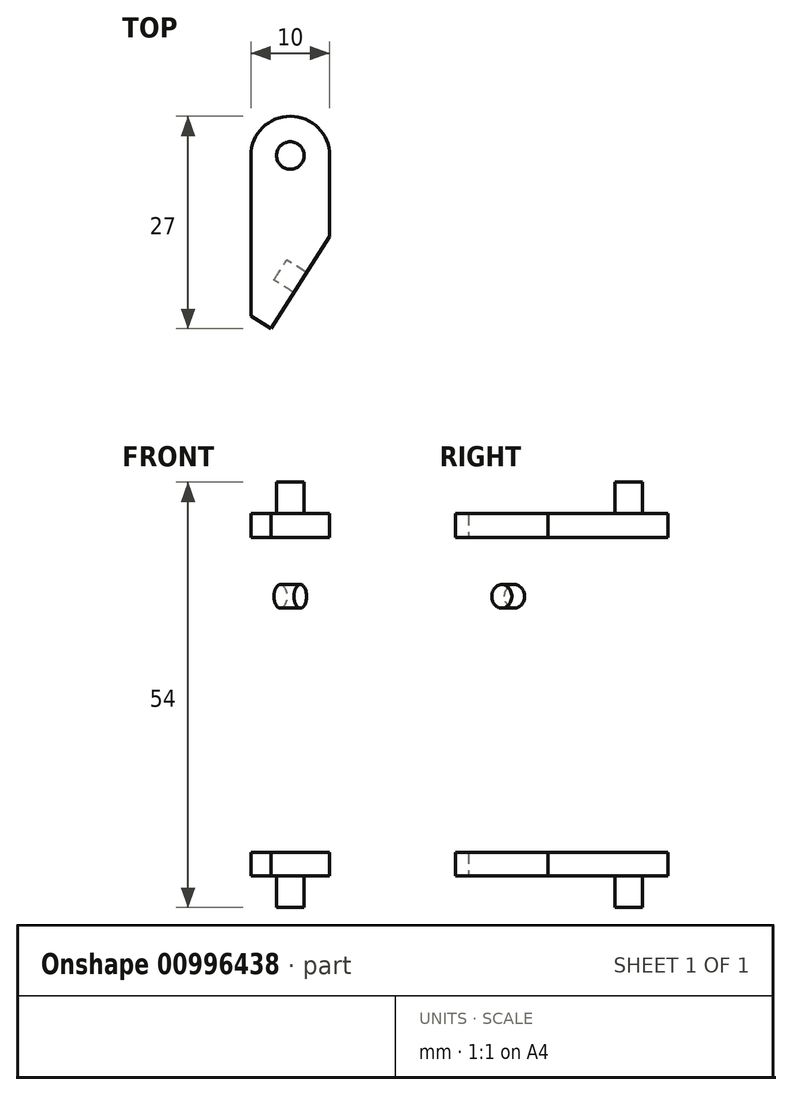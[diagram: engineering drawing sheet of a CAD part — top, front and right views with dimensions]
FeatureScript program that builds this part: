
annotation { "Feature Type Name" : "Feature", "Feature Type Description" : "" }
export const myFeature = defineFeature(function(context is Context, id is Id, definition is map)
    precondition{}
    {
        {
            var Q0;
            Q0=qCreatedBy(makeId("Top.planeOp"),FACE);
            var sketch = newSketch(context, id + "F0", { "sketchPlane" : qUnion([Q0])});
            skArc(sketch, "E0", {"start": v(5, 0) * mm, "mid": v(0, 5) * mm, "end": v(-5, 0) * mm});
            skCircle(sketch, "E1", {"center": v(0, 0) * mm, "radius": 1.75 * mm});
            skLineSegment(sketch, "E2", {"start": v(-5, 0) * mm, "end": v(-5, -20.39) * mm});
            skLineSegment(sketch, "E3", {"start": v(5, 0) * mm, "end": v(5, -10.27) * mm});
            skLineSegment(sketch, "E4", {"start": v(-5, -20.39) * mm, "end": v(-2.47, -22) * mm});
            skLineSegment(sketch, "E5", {"start": v(-2.47, -22) * mm, "end": v(5, -10.27) * mm});
            skLineSegment(sketch, "E6", {"start": v(0, 5) * mm, "end": v(0, -22) * mm, "construction": true});
            skLineSegment(sketch, "E7", {"start": v(-5, -20.39) * mm, "end": v(2.47, -8.66) * mm});
            skLineSegment(sketch, "E8", {"start": v(2.47, -8.66) * mm, "end": v(5, -10.27) * mm});
            skSolve(sketch);
        }
        {
            var Q0;
            Q0=makeQuery(id+"F0.imprint","IMPRINT",FACE,{"disambiguationData":[TD([[makeQuery(id+"F0.imprint","IMPRINT",EDGE,{"derivedFrom":sQuery(id+"F0.wireOp",EDGE,"E4")}),1.0]])]});
            var Q1;
            Q1=makeQuery(id+"F0.imprint","IMPRINT",FACE,{"disambiguationData":[TD([[makeQuery(id+"F0.imprint","IMPRINT",EDGE,{"derivedFrom":sQuery(id+"F0.wireOp",EDGE,"E0")}),1.0]])]});
            extrude(context, id + "F1", {"entities" : qUnion([Q0, Q1]), "flatOperationType" : FlatOperationType.REMOVE, "endBound" : BoundingType.SYMMETRIC, "depth" : 46 * mm, "offsetDistance" : 25 * mm, "domain" : OperationDomain.MODEL});
        }
        {
            var Q0;
            Q0=makeQuery(id+"F0.imprint","IMPRINT",FACE,{"disambiguationData":[TD([[makeQuery(id+"F0.imprint","IMPRINT",EDGE,{"derivedFrom":sQuery(id+"F0.wireOp",EDGE,"E1")}),1.0]])]});
            var Q1;
            Q1=sQuery(id+"F0.wireOp",EDGE,"E1");
            extrude(context, id + "F2", {"entities" : qUnion([Q0]), "operationType" : NewBodyOperationType.ADD, "surfaceOperationType" : NewSurfaceOperationType.ADD, "flatOperationType" : FlatOperationType.REMOVE, "surfaceEntities" : qUnion([Q1]), "endBound" : BoundingType.SYMMETRIC, "depth" : 54 * mm, "offsetDistance" : 25 * mm, "domain" : OperationDomain.MODEL});
        }
        {
            var Q0;
            Q0=makeQuery(id+"F0.imprint","IMPRINT",FACE,{"disambiguationData":[TD([[makeQuery(id+"F0.imprint","IMPRINT",EDGE,{"derivedFrom":sQuery(id+"F0.wireOp",EDGE,"E0")}),1.0]])]});
            var Q1;
            Q1=makeQuery(id+"F0.imprint","IMPRINT",FACE,{"disambiguationData":[TD([[makeQuery(id+"F0.imprint","IMPRINT",EDGE,{"derivedFrom":sQuery(id+"F0.wireOp",EDGE,"E1")}),1.0]])]});
            extrude(context, id + "F3", {"entities" : qUnion([Q0, Q1]), "operationType" : NewBodyOperationType.REMOVE, "flatOperationType" : FlatOperationType.REMOVE, "endBound" : BoundingType.SYMMETRIC, "oppositeDirection" : true, "depth" : 40 * mm, "offsetDistance" : 25 * mm, "domain" : OperationDomain.MODEL});
        }
        {
            var Q0;
            Q0=makeQuery(id+"F3.boolean.opBoolean","COPY",FACE,{"derivedFrom":makeQuery(id+"F3.opExtrude","SWEPT_FACE",FACE,{"disambiguationData":[OSD([sQuery(id+"F0.wireOp",EDGE,"E7")])]})});
            var sketch = newSketch(context, id + "F4", { "sketchPlane" : qUnion([Q0])});
            skLineSegment(sketch, "E9", {"start": v(5.98, -20) * mm, "end": v(19.88, 20) * mm, "construction": true});
            skLineSegment(sketch, "E10", {"start": v(12.93, 0) * mm, "end": v(5.98, 0) * mm, "construction": true});
            skLineSegment(sketch, "E11", {"start": v(12.93, 0) * mm, "end": v(12.93, -12.5) * mm, "construction": true});
            skCircle(sketch, "E12", {"center": v(12.93, -12.5) * mm, "radius": 1.5 * mm});
            skCircle(sketch, "E13.MirrorC", {"center": v(12.93, 12.5) * mm, "radius": 1.5 * mm});
            skSolve(sketch);
        }
        {
            var Q0;
            Q0=makeQuery(id+"F4.imprint","IMPRINT",FACE,{"disambiguationData":[TD([[makeQuery(id+"F4.imprint","IMPRINT",EDGE,{"derivedFrom":sQuery(id+"F4.wireOp",EDGE,"E12")}),1.0]])]});
            var Q1;
            Q1=makeQuery(id+"F4.imprint","IMPRINT",FACE,{"disambiguationData":[TD([[makeQuery(id+"F4.imprint","IMPRINT",EDGE,{"derivedFrom":sQuery(id+"F4.wireOp",EDGE,"E13.MirrorC")}),-1.0]])]});
            extrude(context, id + "F5", {"entities" : qUnion([Q0, Q1]), "operationType" : NewBodyOperationType.REMOVE, "endBound" : BoundingType.THROUGH_ALL, "oppositeDirection" : true, "depth" : 25 * mm, "offsetDistance" : 25 * mm});
        }
    });
